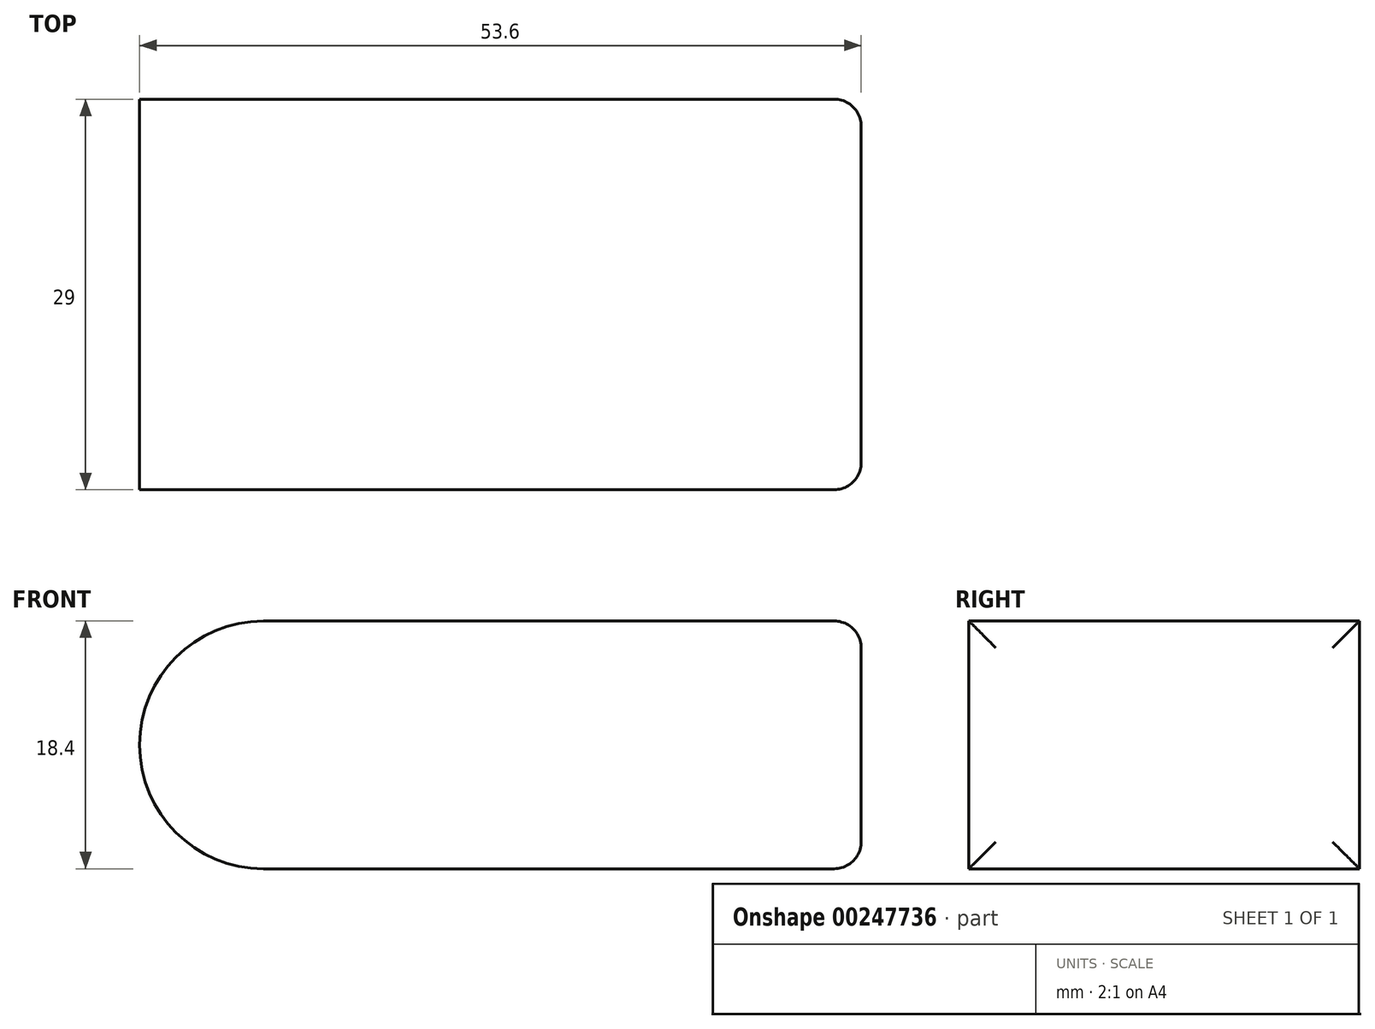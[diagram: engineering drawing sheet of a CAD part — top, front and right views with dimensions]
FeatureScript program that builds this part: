
annotation { "Feature Type Name" : "Feature", "Feature Type Description" : "" }
export const myFeature = defineFeature(function(context is Context, id is Id, definition is map)
    precondition{}
    {
        {
            var Q0;
            Q0=qCreatedBy(makeId("Top.planeOp"),FACE);
            var sketch = newSketch(context, id + "F0", { "sketchPlane" : qUnion([Q0])});
            skLineSegment(sketch, "E0.bottom", {"start": v(-26.8, 14.5) * mm, "end": v(26.8, 14.5) * mm});
            skLineSegment(sketch, "E0.top", {"start": v(-26.8, -14.5) * mm, "end": v(26.8, -14.5) * mm});
            skLineSegment(sketch, "E0.left", {"start": v(-26.8, 14.5) * mm, "end": v(-26.8, -14.5) * mm});
            skLineSegment(sketch, "E0.right", {"start": v(26.8, 14.5) * mm, "end": v(26.8, -14.5) * mm});
            skPoint(sketch, "E0.middle", {"position": v(0, 0) * mm});
            skSolve(sketch);
        }
        {
            var Q0;
            Q0 = qSketchRegion(id + "F0", true);
            extrude(context, id + "F1", {"entities" : qUnion([Q0]), "depth" : 18.4 * mm});
        }
        {
            var Q0;
            Q0=makeQuery(id+"F1.opExtrude","CAP_EDGE",EDGE,{"disambiguationData":[OSD([sQuery(id+"F0.wireOp",EDGE,"E0.left")])],"isStart":false});
            var Q1;
            Q1=makeQuery(id+"F1.opExtrude","CAP_EDGE",EDGE,{"disambiguationData":[OSD([sQuery(id+"F0.wireOp",EDGE,"E0.left")])],"isStart":true});
            fillet(context, id + "F2", {"entities" : qUnion([Q0, Q1]), "radius" : 9.2 * mm, "tangentPropagation" : true, "allowEdgeOverflow" : false});
        }
        {
            var Q0;
            Q0=makeQuery(id+"F1.opExtrude","SWEPT_FACE",FACE,{"disambiguationData":[OSD([sQuery(id+"F0.wireOp",EDGE,"E0.right")])]});
            fillet(context, id + "F3", {"entities" : qUnion([Q0]), "radius" : 2 * mm, "tangentPropagation" : true, "allowEdgeOverflow" : false});
        }
    });
